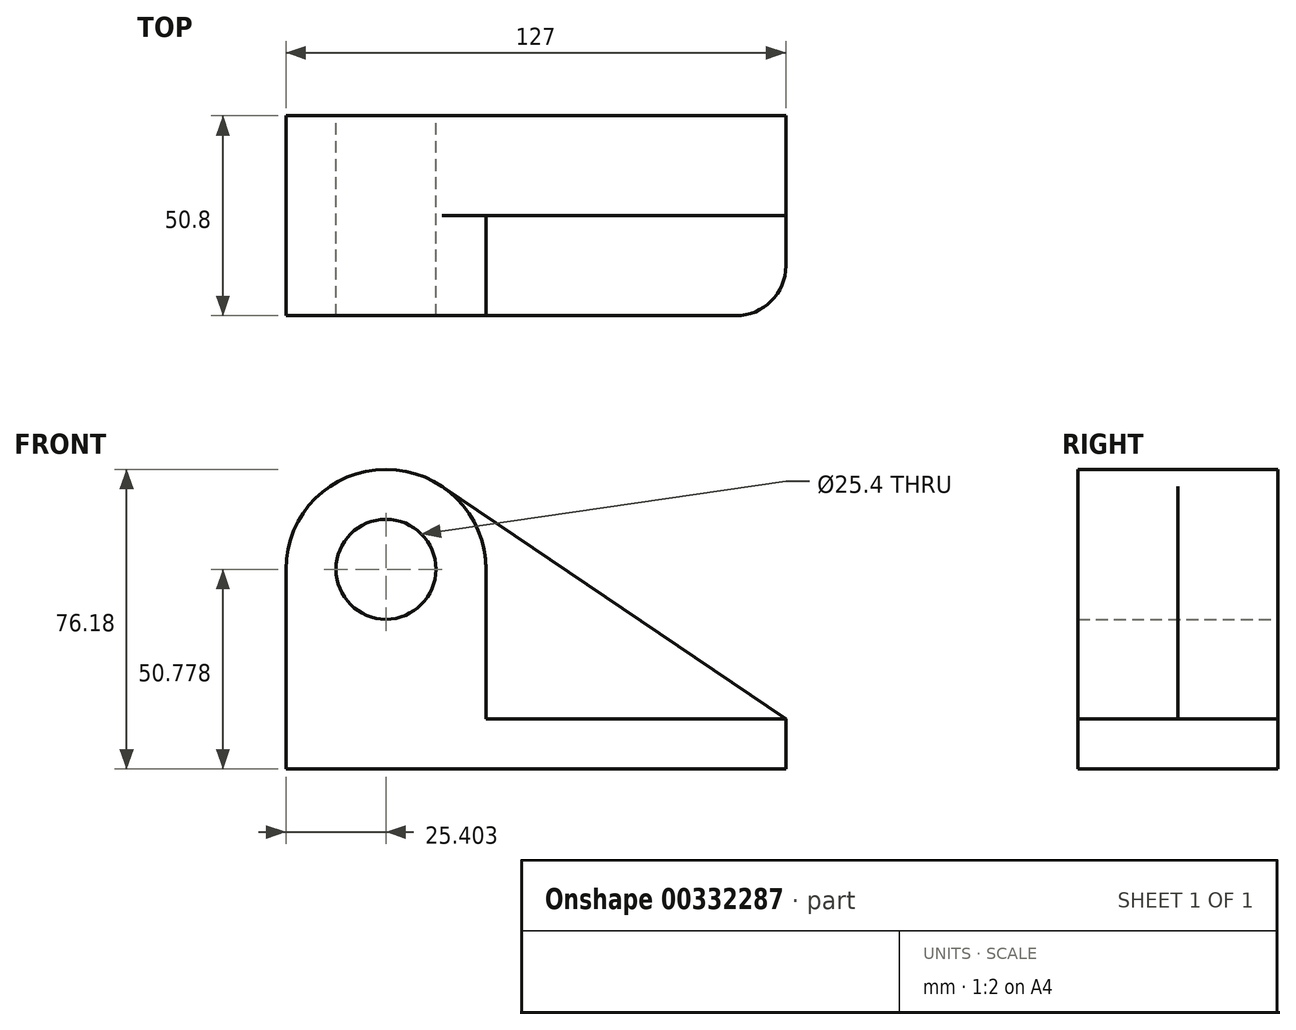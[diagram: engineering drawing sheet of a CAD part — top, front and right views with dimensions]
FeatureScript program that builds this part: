
annotation { "Feature Type Name" : "Feature", "Feature Type Description" : "" }
export const myFeature = defineFeature(function(context is Context, id is Id, definition is map)
    precondition{}
    {
        {
            var Q0;
            Q0=qCreatedBy(makeId("Front.planeOp"),FACE);
            var sketch = newSketch(context, id + "F0", { "sketchPlane" : qUnion([Q0])});
            skArc(sketch, "E0", {"start": v(-24.15, 71.81) * mm, "mid": v(-50.3, 73.21) * mm, "end": v(-63.79, 50.78) * mm});
            skCircle(sketch, "E1", {"center": v(-38.39, 50.78) * mm, "radius": 12.7 * mm});
            skLineSegment(sketch, "E2", {"start": v(-63.79, 50.8) * mm, "end": v(-63.79, 0) * mm});
            skLineSegment(sketch, "E3", {"start": v(-63.79, 0) * mm, "end": v(63.21, 0) * mm});
            skLineSegment(sketch, "E4", {"start": v(63.21, 0) * mm, "end": v(63.21, 12.7) * mm});
            skLineSegment(sketch, "E5", {"start": v(63.21, 12.7) * mm, "end": v(-24.15, 71.81) * mm});
            skSolve(sketch);
        }
        {
            var Q0;
            {var subQ2=sQuery(id+"F0.wireOp",EDGE,"E0");Q0=makeQuery(id+"F0.imprint","IMPRINT",FACE,{"disambiguationData":[TD([[makeQuery(id+"F0.imprint","IMPRINT",EDGE,{"derivedFrom":subQ2}),1.0]])]});}
            extrude(context, id + "F1", {"entities" : qUnion([Q0]), "depth" : 25.4 * mm});
        }
        {
            var Q0;
            Q0=makeQuery(id+"F1.opExtrude","CAP_FACE",FACE,{"disambiguationData":[OSD([sQuery(id+"F0.wireOp",EDGE,"E0"),sQuery(id+"F0.wireOp",EDGE,"E1"),sQuery(id+"F0.wireOp",EDGE,"E2"),sQuery(id+"F0.wireOp",EDGE,"E3"),sQuery(id+"F0.wireOp",EDGE,"E4"),sQuery(id+"F0.wireOp",EDGE,"E5")])],"isStart":false});
            var sketch = newSketch(context, id + "F2", { "sketchPlane" : qUnion([Q0])});
            skCircle(sketch, "E6", {"center": v(-38.39, 50.78) * mm, "radius": 12.7 * mm});
            skArc(sketch, "E7", {"start": v(-12.99, 50.78) * mm, "mid": v(-38.39, 76.18) * mm, "end": v(-63.79, 50.78) * mm});
            skLineSegment(sketch, "E8.bottom", {"start": v(63.21, 12.7) * mm, "end": v(-12.99, 12.7) * mm});
            skLineSegment(sketch, "E8.top", {"start": v(63.21, 0) * mm, "end": v(-63.79, 0) * mm});
            skLineSegment(sketch, "E8.left", {"start": v(63.21, 12.7) * mm, "end": v(63.21, 0) * mm});
            skLineSegment(sketch, "E8.right", {"start": v(-63.79, 12.7) * mm, "end": v(-63.79, 0) * mm});
            skLineSegment(sketch, "E9", {"start": v(-63.79, 50.8) * mm, "end": v(-63.79, 12.7) * mm});
            skLineSegment(sketch, "E10", {"start": v(-12.99, 50.78) * mm, "end": v(-12.99, 12.7) * mm});
            skSolve(sketch);
        }
        {
            var Q0;
            Q0=makeQuery(id+"F2.imprint","IMPRINT",FACE,{"disambiguationData":[TD([[makeQuery(id+"F2.imprint","IMPRINT",EDGE,{"derivedFrom":sQuery(id+"F2.wireOp",EDGE,"E6")}),-1.0]])]});
            extrude(context, id + "F3", {"entities" : qUnion([Q0]), "operationType" : NewBodyOperationType.ADD, "depth" : 25.4 * mm});
        }
        {
            var Q0;
            Q0=makeQuery(id+"F3.opExtrude","CAP_EDGE",EDGE,{"disambiguationData":[OSD([sQuery(id+"F2.wireOp",EDGE,"E8.left")])],"isStart":false});
            fillet(context, id + "F4", {"entities" : qUnion([Q0]), "radius" : 12.7 * mm, "tangentPropagation" : true, "allowEdgeOverflow" : false});
        }
    });
